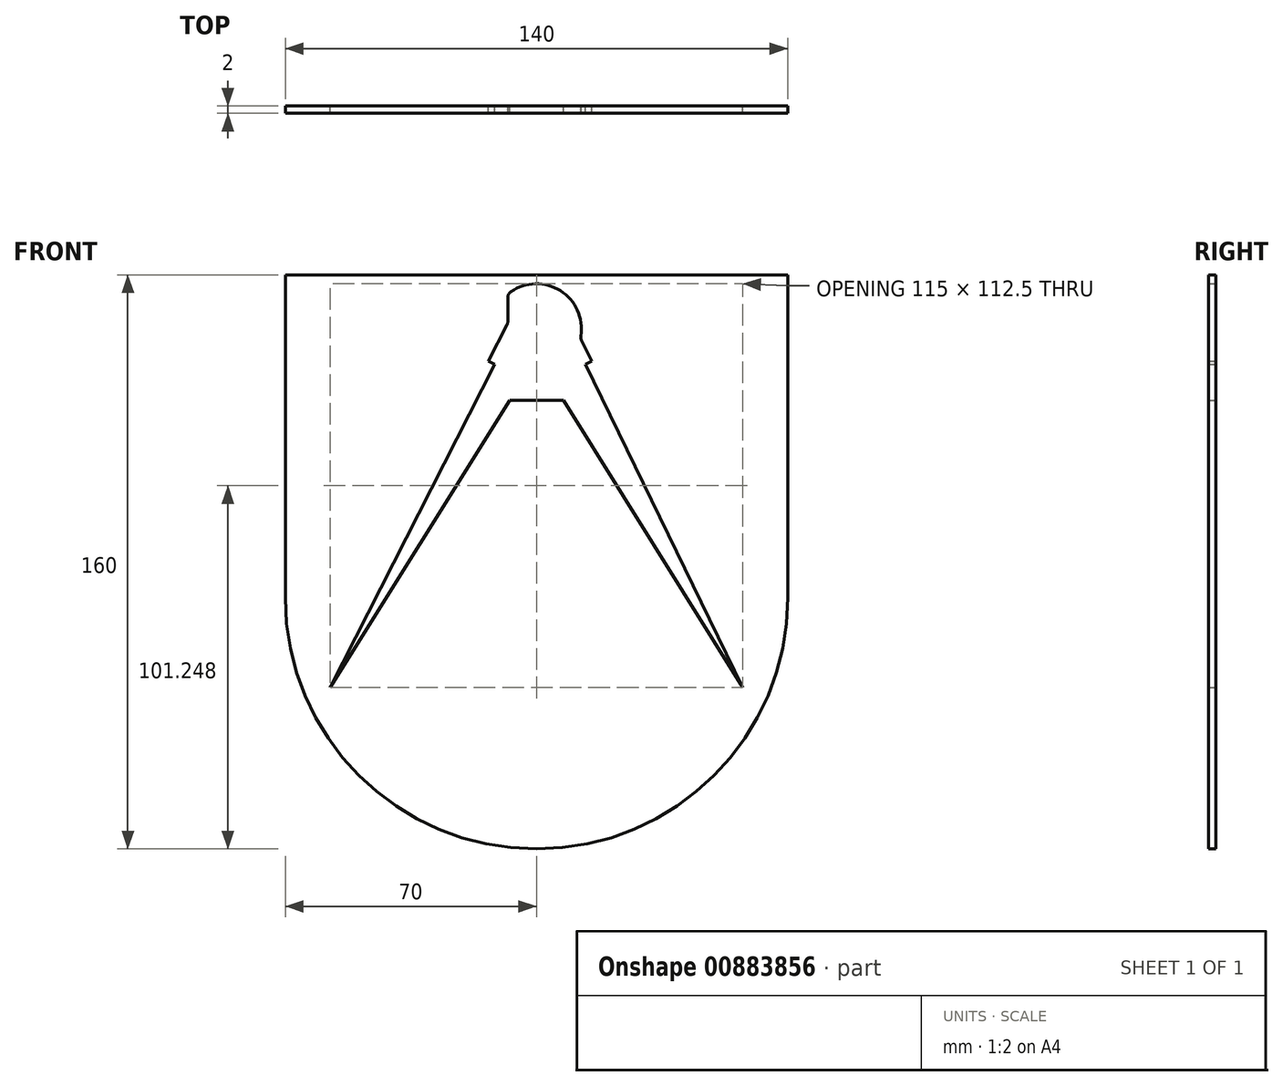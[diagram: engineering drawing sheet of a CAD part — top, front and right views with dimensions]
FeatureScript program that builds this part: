
annotation { "Feature Type Name" : "Feature", "Feature Type Description" : "" }
export const myFeature = defineFeature(function(context is Context, id is Id, definition is map)
    precondition{}
    {
        {
            var Q0;
            Q0=qCreatedBy(makeId("Front.planeOp"),FACE);
            var sketch = newSketch(context, id + "F0", { "sketchPlane" : qUnion([Q0])});
            skLineSegment(sketch, "E0", {"start": v(-70, 90) * mm, "end": v(70, 90) * mm});
            skLineSegment(sketch, "E1", {"start": v(70, 90) * mm, "end": v(70, 0) * mm});
            skLineSegment(sketch, "E2", {"start": v(-70, 90) * mm, "end": v(-70, 0) * mm});
            skArc(sketch, "E3", {"start": v(-70, 0) * mm, "mid": v(0, -70) * mm, "end": v(70, 0) * mm});
            skSolve(sketch);
        }
        {
            var Q0;
            Q0 = qSketchRegion(id + "F0", true);
            extrude(context, id + "F1", {"entities" : qUnion([Q0]), "depth" : 2 * mm, "offsetDistance" : 25 * mm});
        }
        {
            var Q0;
            Q0=qCreatedBy(makeId("Front.planeOp"),FACE);
            var sketch = newSketch(context, id + "F2", { "sketchPlane" : qUnion([Q0])});
            skLineSegment(sketch, "E4", {"start": v(-11.63, 65) * mm, "end": v(-57.5, -25) * mm});
            skLineSegment(sketch, "E5", {"start": v(-57.5, -25) * mm, "end": v(-7.5, 55) * mm});
            skLineSegment(sketch, "E6", {"start": v(7.5, 55) * mm, "end": v(57.5, -25) * mm});
            skLineSegment(sketch, "E7", {"start": v(57.5, -25) * mm, "end": v(13.6, 65) * mm});
            skLineSegment(sketch, "E8", {"start": v(-7.5, 55) * mm, "end": v(7.5, 55) * mm});
            skLineSegment(sketch, "E9", {"start": v(-57.5, -25) * mm, "end": v(57.5, -25) * mm, "construction": true});
            skArc(sketch, "E10", {"start": v(12.34, 72.98) * mm, "mid": v(6.67, 85.57) * mm, "end": v(-7.14, 85.26) * mm});
            skLineSegment(sketch, "E11", {"start": v(-13.41, 65.9) * mm, "end": v(-8.22, 76.1) * mm});
            skLineSegment(sketch, "E12", {"start": v(-8, 77.01) * mm, "end": v(-8, 83.62) * mm});
            skLineSegment(sketch, "E13", {"start": v(13.6, 65) * mm, "end": v(15.4, 65.88) * mm});
            skLineSegment(sketch, "E14", {"start": v(15.4, 65.88) * mm, "end": v(12.51, 71.78) * mm});
            skPoint(sketch, "E15.visualSharp", {"position": v(-8, 84.6) * mm});
            skArc(sketch, "E15.filletArc", {"start": v(-7.14, 85.26) * mm, "mid": v(-7.77, 84.54) * mm, "end": v(-8, 83.62) * mm});
            skPoint(sketch, "E16.visualSharp", {"position": v(12.22, 72.37) * mm});
            skArc(sketch, "E16.filletArc", {"start": v(12.34, 72.98) * mm, "mid": v(12.33, 72.37) * mm, "end": v(12.51, 71.78) * mm});
            skPoint(sketch, "E17.visualSharp", {"position": v(-8, 76.53) * mm});
            skArc(sketch, "E17.filletArc", {"start": v(-8.22, 76.1) * mm, "mid": v(-8.06, 76.54) * mm, "end": v(-8, 77.01) * mm});
            skLineSegment(sketch, "E18", {"start": v(-11.63, 65) * mm, "end": v(-13.41, 65.9) * mm});
            skLineSegment(sketch, "E19", {"start": v(-11.63, 65) * mm, "end": v(13.6, 65) * mm, "construction": true});
            skSolve(sketch);
        }
        {
            var Q0;
            Q0 = qSketchRegion(id + "F2", true);
            var Q1;
            Q1=makeQuery(id+"F1.opExtrude","CAP_FACE",FACE,{"disambiguationData":[OSD([sQuery(id+"F0.wireOp",EDGE,"E0"),sQuery(id+"F0.wireOp",EDGE,"E1"),sQuery(id+"F0.wireOp",EDGE,"E2"),sQuery(id+"F0.wireOp",EDGE,"E3")])],"isStart":false});
            extrude(context, id + "F3", {"entities" : qUnion([Q0]), "operationType" : NewBodyOperationType.REMOVE, "endBound" : BoundingType.UP_TO_SURFACE, "depth" : 25 * mm, "endBoundEntityFace" : qUnion([Q1]), "offsetDistance" : 25 * mm});
        }
    });
